# Revit family: Shower-Valve_Trim-KOHLER-Pitch-K-TS74042
name_source: partatom
category: Specialty Equipment
units: mm (PartAtom-declared; Revit-internal decimal feet)

## family parameters
Cut with Voids When Loaded = No
Host = Face
Maintain Annotation Orientation = No
OmniClass Number = 23.31.25.00
OmniClass Title = Toilet and Bath Specialties
Part Type = Normal
Room Calculation Point = No
Round Connector Dimension = Use Diameter
Shared = No

## types (4) — shared parameters
ADA Compliant = Yes
Assembly Code = C1030200
Date Modified = 04/19/2022
Default Elevation = 42"
Description = Rite-Temp shower valve trim
Handle Clearance = 3 3/8"
Height = 6 3/8"
Length = 3 11/16"
Manufacturer = Kohler Co.
Master Format 2014 = 10 28 00
Master Format 2014 Name = Toilet, Bath, and Laundry Accessories
Material = Premium Metal Construction
Product Documentation Link = https://www.us.kohler.com
Product Name = Pitch
Product Page URL = https://www.us.kohler.com
URL = https://www.us.kohler.com
WaterSense Certified = No
Width = 6 3/8"

## per-type parameters (varying)
| type | Finish | Model | Type |
| CP-Polished Chrome | Kohler-Metal-CP-Polished_Chrome | K-TS74042-4-CP | 4 |
| BN-Vibrant Brushed Nickel | Kohler-Metal-BN-Vibrant_Brushed_Nickel | K-TS74042-4-BN | 3 |
| BL-Matte Black | Kohler-Metal-BL-Matte_Black | K-TS74042-4-BL | 2 |
| 2MB-Vibrant Brushed Moderne Brass | Kohler-Metal-2MB-Vibrant_Brushed_Moderne_Brass | K-TS74042-4-2MB | 1 |

## geometry (parser evidence)
native form markers: Sweep x6
no freeform markers — native parametric forms only
